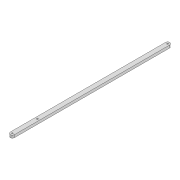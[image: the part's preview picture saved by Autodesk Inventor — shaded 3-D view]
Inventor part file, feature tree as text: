
AUTODESK INVENTOR PART (.ipt)
format: ipt  version: 2022 (Build 260153000, 153)  size: 92,160 bytes
history: native  units: mm
features: extrude x1, sketch x1
ambient origin geometry x8: Origin, YZ Plane, XZ Plane, XY Plane, X Axis, Y Axis, Z Axis, Center Point
bodies: Solid1 (feature_tree)
feature tree (2):
  extrude  "Extrusion1"  Depth=57.376mm
  sketch  "Sketch1"  dims[d0=3.3mm d1=3.3mm d2=10.0mm d3=355.998mm d6=6.0mm d7=0.0mm d14=3.3mm d15=57.376mm]
